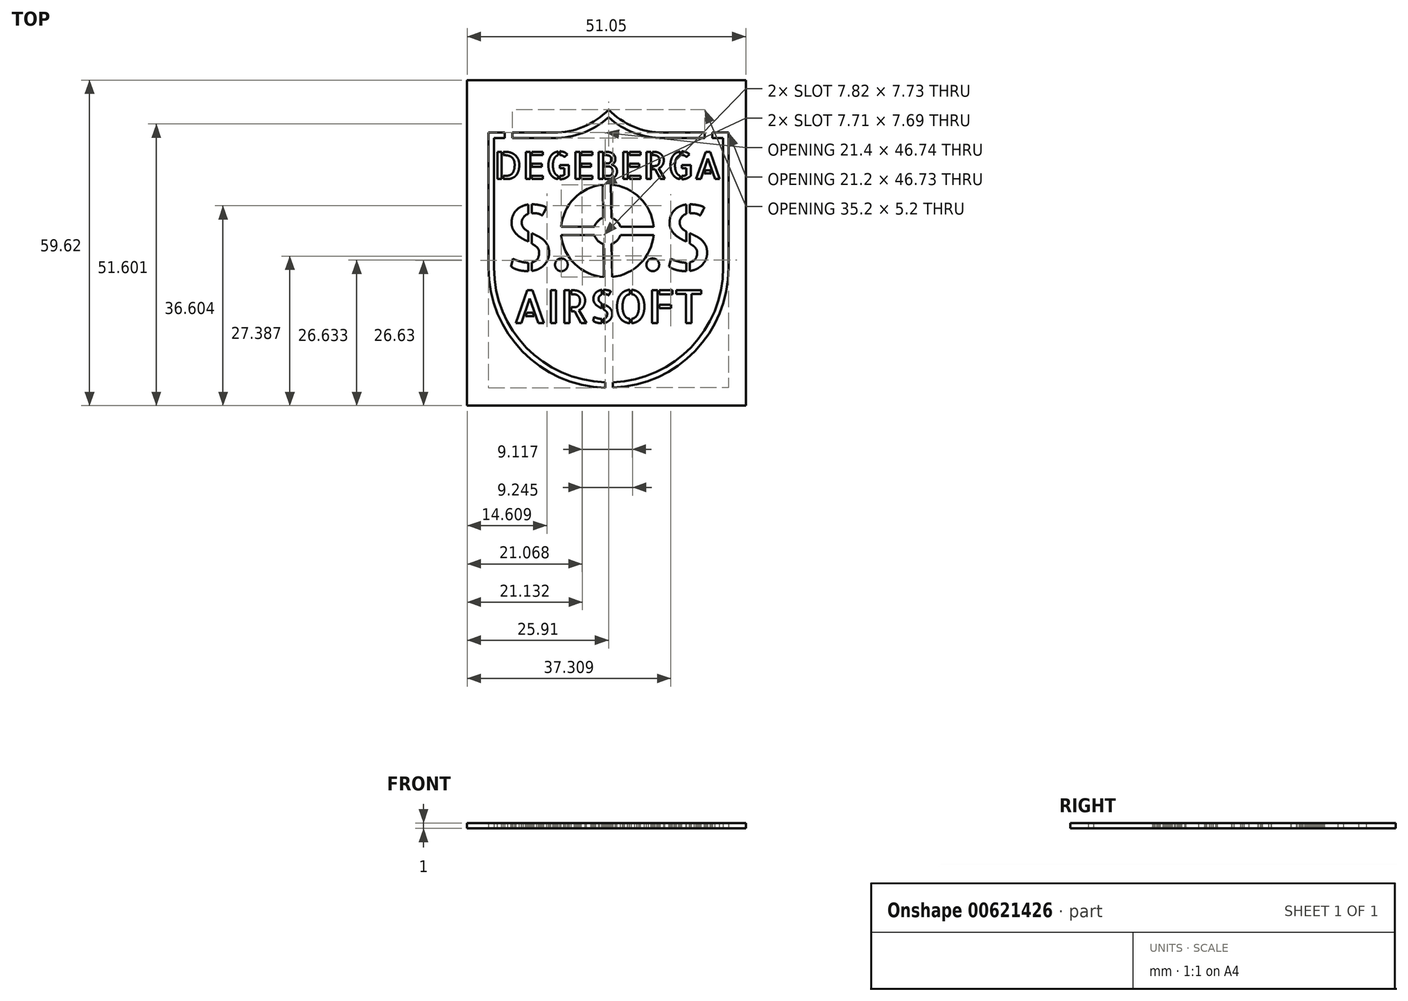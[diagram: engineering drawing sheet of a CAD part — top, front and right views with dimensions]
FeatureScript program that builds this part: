
annotation { "Feature Type Name" : "Feature", "Feature Type Description" : "" }
export const myFeature = defineFeature(function(context is Context, id is Id, definition is map)
    precondition{}
    {
        {
            var Q0;
            Q0=qCreatedBy(makeId("Top.planeOp"),FACE);
            var sketch = newSketch(context, id + "F0", { "sketchPlane" : qUnion([Q0])});
            skLineSegment(sketch, "E0.bottom", {"start": v(-46.46, 42.23) * mm, "end": v(53.54, 42.23) * mm});
            skLineSegment(sketch, "E0.top", {"start": v(-46.46, -77.77) * mm, "end": v(53.54, -77.77) * mm});
            skLineSegment(sketch, "E0.left", {"start": v(-46.46, 42.23) * mm, "end": v(-46.46, -77.77) * mm});
            skLineSegment(sketch, "E0.right", {"start": v(53.54, 42.23) * mm, "end": v(53.54, -77.77) * mm});
            skArc(sketch, "E1", {"start": v(-22, -24.75) * mm, "mid": v(-15.77, -40.09) * mm, "end": v(-0.6, -46.74) * mm});
            skLineSegment(sketch, "E2", {"start": v(-22, -24.75) * mm, "end": v(-22, 0) * mm});
            skLineSegment(sketch, "E3", {"start": v(22, -24.75) * mm, "end": v(22, 0) * mm});
            skLineSegment(sketch, "E4", {"start": v(-22, 0) * mm, "end": v(-19, 0) * mm});
            skLineSegment(sketch, "E5", {"start": v(22, 0) * mm, "end": v(19, 0) * mm});
            skArc(sketch, "E6", {"start": v(-10, 0) * mm, "mid": v(-4.58, 1.1) * mm, "end": v(0, 4.2) * mm});
            skArc(sketch, "E7", {"start": v(0, 4.2) * mm, "mid": v(4.58, 1.1) * mm, "end": v(10, 0) * mm});
            skArc(sketch, "E8", {"start": v(-21, -24.75) * mm, "mid": v(-15.06, -39.38) * mm, "end": v(-0.6, -45.74) * mm});
            skLineSegment(sketch, "E9", {"start": v(-21, -24.75) * mm, "end": v(-21, -1) * mm});
            skLineSegment(sketch, "E10", {"start": v(-21, -1) * mm, "end": v(-19, -1) * mm});
            skLineSegment(sketch, "E11", {"start": v(21, -24.75) * mm, "end": v(21, -1) * mm});
            skLineSegment(sketch, "E12", {"start": v(21, -1) * mm, "end": v(19, -1) * mm});
            skArc(sketch, "E13", {"start": v(-10, -1) * mm, "mid": v(-4.65, -0.01) * mm, "end": v(0, 2.82) * mm});
            skArc(sketch, "E14", {"start": v(0, 2.82) * mm, "mid": v(4.65, -0.01) * mm, "end": v(10, -1) * mm});
            skLineSegment(sketch, "E15.left", {"start": v(-19, 0) * mm, "end": v(-19, -1) * mm});
            skLineSegment(sketch, "E15.right", {"start": v(-17.6, 0) * mm, "end": v(-17.6, -1) * mm});
            skLineSegment(sketch, "E16.left", {"start": v(17.6, 0) * mm, "end": v(17.6, -1) * mm});
            skLineSegment(sketch, "E16.right", {"start": v(19, 0) * mm, "end": v(19, -1) * mm});
            skLineSegment(sketch, "E17", {"start": v(-0.6, -45.74) * mm, "end": v(-0.6, -46.74) * mm});
            skLineSegment(sketch, "E18", {"start": v(0.8, -45.73) * mm, "end": v(0.8, -46.73) * mm});
            skArc(sketch, "E19.trimOffspring", {"start": v(0.8, -45.73) * mm, "mid": v(15.13, -39.31) * mm, "end": v(21, -24.75) * mm});
            skArc(sketch, "E20.trimOffspring", {"start": v(0.8, -46.73) * mm, "mid": v(15.84, -40.02) * mm, "end": v(22, -24.75) * mm});
            skLineSegment(sketch, "E21.trimOffspring", {"start": v(17.6, -1) * mm, "end": v(10, -1) * mm});
            skLineSegment(sketch, "E22.trimOffspring", {"start": v(17.6, 0) * mm, "end": v(10, 0) * mm});
            skLineSegment(sketch, "E23.trimOffspring", {"start": v(-17.6, 0) * mm, "end": v(-10, 0) * mm});
            skLineSegment(sketch, "E24.trimOffspring", {"start": v(-17.6, -1) * mm, "end": v(-10, -1) * mm});
            skSolve(sketch);
        }
        {
            var Q0;
            Q0 = qSketchRegion(id + "F0", true);
            var Q1;
            Q1=makeQuery(id+"F0.imprint","IMPRINT",FACE,{"disambiguationData":[TD([[makeQuery(id+"F0.imprint","IMPRINT",EDGE,{"derivedFrom":sQuery(id+"F0.wireOp",EDGE,"E8")}),1.0]])]});
            extrude(context, id + "F1", {"entities" : qUnion([Q0, Q1]), "depth" : 1 * mm, "offsetDistance" : 25 * mm});
        }
        {
            var Q0;
            Q0=makeQuery(id+"F1.opExtrude","CAP_FACE",FACE,{"disambiguationData":[OSD([sQuery(id+"F0.wireOp",EDGE,"E0.bottom"),sQuery(id+"F0.wireOp",EDGE,"E0.top"),sQuery(id+"F0.wireOp",EDGE,"E0.left"),sQuery(id+"F0.wireOp",EDGE,"E0.right"),sQuery(id+"F0.wireOp",EDGE,"E1"),sQuery(id+"F0.wireOp",EDGE,"E2"),sQuery(id+"F0.wireOp",EDGE,"E3"),sQuery(id+"F0.wireOp",EDGE,"E4"),sQuery(id+"F0.wireOp",EDGE,"E5"),sQuery(id+"F0.wireOp",EDGE,"E6"),sQuery(id+"F0.wireOp",EDGE,"E7"),sQuery(id+"F0.wireOp",EDGE,"E8"),sQuery(id+"F0.wireOp",EDGE,"E9"),sQuery(id+"F0.wireOp",EDGE,"E10"),sQuery(id+"F0.wireOp",EDGE,"E11"),sQuery(id+"F0.wireOp",EDGE,"E12"),sQuery(id+"F0.wireOp",EDGE,"E13"),sQuery(id+"F0.wireOp",EDGE,"E14"),sQuery(id+"F0.wireOp",EDGE,"E15.left"),sQuery(id+"F0.wireOp",EDGE,"E15.right"),sQuery(id+"F0.wireOp",EDGE,"E16.left"),sQuery(id+"F0.wireOp",EDGE,"E16.right"),sQuery(id+"F0.wireOp",EDGE,"E17"),sQuery(id+"F0.wireOp",EDGE,"E18"),sQuery(id+"F0.wireOp",EDGE,"E19.trimOffspring"),sQuery(id+"F0.wireOp",EDGE,"E20.trimOffspring"),sQuery(id+"F0.wireOp",EDGE,"E21.trimOffspring"),sQuery(id+"F0.wireOp",EDGE,"E22.trimOffspring"),sQuery(id+"F0.wireOp",EDGE,"E23.trimOffspring"),sQuery(id+"F0.wireOp",EDGE,"E24.trimOffspring")])],"isStart":false});
            var sketch = newSketch(context, id + "F2", { "sketchPlane" : qUnion([Q0])});
            skText(sketch, "E25", { "text": "S.   .S", "fontName": "AllertaStencil-Regular.ttf"});
            const initialGuessF2  = {"E25": [-0.01917, -0.02531, 1, 0, 0.012]};
            skSetInitialGuess(sketch, initialGuessF2);
            skSolve(sketch);
        }
        {
            var Q0;
            Q0 = qSketchRegion(id + "F2", true);
            extrude(context, id + "F3", {"entities" : qUnion([Q0]), "operationType" : NewBodyOperationType.REMOVE, "oppositeDirection" : true, "depth" : 25 * mm, "offsetDistance" : 25 * mm});
        }
        {
            var Q0;
            Q0=makeQuery(id+"F1.opExtrude","CAP_FACE",FACE,{"disambiguationData":[OSD([sQuery(id+"F0.wireOp",EDGE,"E0.bottom"),sQuery(id+"F0.wireOp",EDGE,"E0.top"),sQuery(id+"F0.wireOp",EDGE,"E0.left"),sQuery(id+"F0.wireOp",EDGE,"E0.right"),sQuery(id+"F0.wireOp",EDGE,"E1"),sQuery(id+"F0.wireOp",EDGE,"E2"),sQuery(id+"F0.wireOp",EDGE,"E3"),sQuery(id+"F0.wireOp",EDGE,"E4"),sQuery(id+"F0.wireOp",EDGE,"E5"),sQuery(id+"F0.wireOp",EDGE,"E6"),sQuery(id+"F0.wireOp",EDGE,"E7"),sQuery(id+"F0.wireOp",EDGE,"E8"),sQuery(id+"F0.wireOp",EDGE,"E9"),sQuery(id+"F0.wireOp",EDGE,"E10"),sQuery(id+"F0.wireOp",EDGE,"E11"),sQuery(id+"F0.wireOp",EDGE,"E12"),sQuery(id+"F0.wireOp",EDGE,"E13"),sQuery(id+"F0.wireOp",EDGE,"E14"),sQuery(id+"F0.wireOp",EDGE,"E15.left"),sQuery(id+"F0.wireOp",EDGE,"E15.right"),sQuery(id+"F0.wireOp",EDGE,"E16.left"),sQuery(id+"F0.wireOp",EDGE,"E16.right"),sQuery(id+"F0.wireOp",EDGE,"E17"),sQuery(id+"F0.wireOp",EDGE,"E18"),sQuery(id+"F0.wireOp",EDGE,"E19.trimOffspring"),sQuery(id+"F0.wireOp",EDGE,"E20.trimOffspring"),sQuery(id+"F0.wireOp",EDGE,"E21.trimOffspring"),sQuery(id+"F0.wireOp",EDGE,"E22.trimOffspring"),sQuery(id+"F0.wireOp",EDGE,"E23.trimOffspring"),sQuery(id+"F0.wireOp",EDGE,"E24.trimOffspring")])],"isStart":false});
            var sketch = newSketch(context, id + "F4", { "sketchPlane" : qUnion([Q0])});
            skCircle(sketch, "E26", {"center": v(-0.22, -18) * mm, "radius": 8.5 * mm});
            skCircle(sketch, "E27", {"center": v(-0.22, -18) * mm, "radius": 2.5 * mm});
            skLineSegment(sketch, "E28.left", {"start": v(-1.07, -9.54) * mm, "end": v(-0.87, -26.48) * mm});
            skLineSegment(sketch, "E28.right", {"start": v(0.43, -9.52) * mm, "end": v(0.63, -26.46) * mm});
            skLineSegment(sketch, "E29.bottom", {"start": v(-8.69, -17.25) * mm, "end": v(8.25, -17.25) * mm});
            skLineSegment(sketch, "E29.top", {"start": v(-8.69, -18.75) * mm, "end": v(8.25, -18.75) * mm});
            skSolve(sketch);
        }
        {
            var Q0;
            {var subQ0=sQuery(id+"F4.wireOp",EDGE,"E28.right");var subQ1=sQuery(id+"F4.wireOp",EDGE,"E26");var subQ2=makeQuery(id+"F4.imprint","INTERSECT",VERTEX,{"disambiguationData":[OD(0.0)],"derivedFrom":[subQ1,subQ0]});Q0=makeQuery(id+"F4.imprint","IMPRINT",FACE,{"disambiguationData":[TD([[makeQuery(id+"F4.imprint","IMPRINT",EDGE,{"disambiguationData":[TD([[subQ2,1.0]])],"derivedFrom":subQ1}),1.0]])]});}
            var Q1;
            {var subQ0=sQuery(id+"F4.wireOp",EDGE,"E28.left");var subQ1=sQuery(id+"F4.wireOp",EDGE,"E26");var subQ2=makeQuery(id+"F4.imprint","INTERSECT",VERTEX,{"disambiguationData":[OD(0.0)],"derivedFrom":[subQ1,subQ0]});Q1=makeQuery(id+"F4.imprint","IMPRINT",FACE,{"disambiguationData":[TD([[makeQuery(id+"F4.imprint","IMPRINT",EDGE,{"disambiguationData":[TD([[subQ2,-1.0]])],"derivedFrom":subQ1}),1.0]])]});}
            var Q2;
            {var subQ0=sQuery(id+"F4.wireOp",EDGE,"E28.left");var subQ1=sQuery(id+"F4.wireOp",EDGE,"E26");var subQ2=makeQuery(id+"F4.imprint","INTERSECT",VERTEX,{"disambiguationData":[OD(1.0)],"derivedFrom":[subQ1,subQ0]});Q2=makeQuery(id+"F4.imprint","IMPRINT",FACE,{"disambiguationData":[TD([[makeQuery(id+"F4.imprint","IMPRINT",EDGE,{"disambiguationData":[TD([[subQ2,1.0]])],"derivedFrom":subQ1}),1.0]])]});}
            var Q3;
            {var subQ0=sQuery(id+"F4.wireOp",EDGE,"E28.right");var subQ1=sQuery(id+"F4.wireOp",EDGE,"E26");var subQ2=makeQuery(id+"F4.imprint","INTERSECT",VERTEX,{"disambiguationData":[OD(1.0)],"derivedFrom":[subQ1,subQ0]});Q3=makeQuery(id+"F4.imprint","IMPRINT",FACE,{"disambiguationData":[TD([[makeQuery(id+"F4.imprint","IMPRINT",EDGE,{"disambiguationData":[TD([[subQ2,-1.0]])],"derivedFrom":subQ1}),1.0]])]});}
            extrude(context, id + "F5", {"entities" : qUnion([Q0, Q1, Q2, Q3]), "operationType" : NewBodyOperationType.REMOVE, "oppositeDirection" : true, "depth" : 25 * mm, "offsetDistance" : 25 * mm});
        }
        {
            var Q0;
            Q0=makeQuery(id+"F1.opExtrude","CAP_FACE",FACE,{"disambiguationData":[OSD([sQuery(id+"F0.wireOp",EDGE,"E0.bottom"),sQuery(id+"F0.wireOp",EDGE,"E0.top"),sQuery(id+"F0.wireOp",EDGE,"E0.left"),sQuery(id+"F0.wireOp",EDGE,"E0.right"),sQuery(id+"F0.wireOp",EDGE,"E1"),sQuery(id+"F0.wireOp",EDGE,"E2"),sQuery(id+"F0.wireOp",EDGE,"E3"),sQuery(id+"F0.wireOp",EDGE,"E4"),sQuery(id+"F0.wireOp",EDGE,"E5"),sQuery(id+"F0.wireOp",EDGE,"E6"),sQuery(id+"F0.wireOp",EDGE,"E7"),sQuery(id+"F0.wireOp",EDGE,"E8"),sQuery(id+"F0.wireOp",EDGE,"E9"),sQuery(id+"F0.wireOp",EDGE,"E10"),sQuery(id+"F0.wireOp",EDGE,"E11"),sQuery(id+"F0.wireOp",EDGE,"E12"),sQuery(id+"F0.wireOp",EDGE,"E13"),sQuery(id+"F0.wireOp",EDGE,"E14"),sQuery(id+"F0.wireOp",EDGE,"E15.left"),sQuery(id+"F0.wireOp",EDGE,"E15.right"),sQuery(id+"F0.wireOp",EDGE,"E16.left"),sQuery(id+"F0.wireOp",EDGE,"E16.right"),sQuery(id+"F0.wireOp",EDGE,"E17"),sQuery(id+"F0.wireOp",EDGE,"E18"),sQuery(id+"F0.wireOp",EDGE,"E19.trimOffspring"),sQuery(id+"F0.wireOp",EDGE,"E20.trimOffspring"),sQuery(id+"F0.wireOp",EDGE,"E21.trimOffspring"),sQuery(id+"F0.wireOp",EDGE,"E22.trimOffspring"),sQuery(id+"F0.wireOp",EDGE,"E23.trimOffspring"),sQuery(id+"F0.wireOp",EDGE,"E24.trimOffspring")])],"isStart":false});
            var sketch = newSketch(context, id + "F6", { "sketchPlane" : qUnion([Q0])});
            skText(sketch, "E30", { "text": "DEGEBERGA", "fontName": "AllertaStencil-Regular.ttf"});
            const initialGuessF6  = {"E30": [-0.02104, -0.0085, 1, 0, 0.005]};
            skSetInitialGuess(sketch, initialGuessF6);
            skSolve(sketch);
        }
        {
            var Q0;
            Q0 = qSketchRegion(id + "F6", true);
            extrude(context, id + "F7", {"entities" : qUnion([Q0]), "operationType" : NewBodyOperationType.REMOVE, "oppositeDirection" : true, "depth" : 25 * mm, "offsetDistance" : 25 * mm});
        }
        {
            var Q0;
            Q0=makeQuery(id+"F1.opExtrude","CAP_FACE",FACE,{"disambiguationData":[OSD([sQuery(id+"F0.wireOp",EDGE,"E0.bottom"),sQuery(id+"F0.wireOp",EDGE,"E0.top"),sQuery(id+"F0.wireOp",EDGE,"E0.left"),sQuery(id+"F0.wireOp",EDGE,"E0.right"),sQuery(id+"F0.wireOp",EDGE,"E1"),sQuery(id+"F0.wireOp",EDGE,"E2"),sQuery(id+"F0.wireOp",EDGE,"E3"),sQuery(id+"F0.wireOp",EDGE,"E4"),sQuery(id+"F0.wireOp",EDGE,"E5"),sQuery(id+"F0.wireOp",EDGE,"E6"),sQuery(id+"F0.wireOp",EDGE,"E7"),sQuery(id+"F0.wireOp",EDGE,"E8"),sQuery(id+"F0.wireOp",EDGE,"E9"),sQuery(id+"F0.wireOp",EDGE,"E10"),sQuery(id+"F0.wireOp",EDGE,"E11"),sQuery(id+"F0.wireOp",EDGE,"E12"),sQuery(id+"F0.wireOp",EDGE,"E13"),sQuery(id+"F0.wireOp",EDGE,"E14"),sQuery(id+"F0.wireOp",EDGE,"E15.left"),sQuery(id+"F0.wireOp",EDGE,"E15.right"),sQuery(id+"F0.wireOp",EDGE,"E16.left"),sQuery(id+"F0.wireOp",EDGE,"E16.right"),sQuery(id+"F0.wireOp",EDGE,"E17"),sQuery(id+"F0.wireOp",EDGE,"E18"),sQuery(id+"F0.wireOp",EDGE,"E19.trimOffspring"),sQuery(id+"F0.wireOp",EDGE,"E20.trimOffspring"),sQuery(id+"F0.wireOp",EDGE,"E21.trimOffspring"),sQuery(id+"F0.wireOp",EDGE,"E22.trimOffspring"),sQuery(id+"F0.wireOp",EDGE,"E23.trimOffspring"),sQuery(id+"F0.wireOp",EDGE,"E24.trimOffspring")])],"isStart":false});
            var sketch = newSketch(context, id + "F8", { "sketchPlane" : qUnion([Q0])});
            skText(sketch, "E31", { "text": "AIRSOFT", "fontName": "AllertaStencil-Regular.ttf"});
            const initialGuessF8  = {"E31": [-0.01753, -0.03488, 1, 0, 0.006]};
            skSetInitialGuess(sketch, initialGuessF8);
            skSolve(sketch);
        }
        {
            var Q0;
            Q0 = qSketchRegion(id + "F8", true);
            extrude(context, id + "F9", {"entities" : qUnion([Q0]), "operationType" : NewBodyOperationType.REMOVE, "oppositeDirection" : true, "depth" : 25 * mm, "offsetDistance" : 25 * mm});
        }
        {
            var Q0;
            Q0=makeQuery(id+"F1.opExtrude","CAP_FACE",FACE,{"disambiguationData":[OSD([sQuery(id+"F0.wireOp",EDGE,"E0.bottom"),sQuery(id+"F0.wireOp",EDGE,"E0.top"),sQuery(id+"F0.wireOp",EDGE,"E0.left"),sQuery(id+"F0.wireOp",EDGE,"E0.right"),sQuery(id+"F0.wireOp",EDGE,"E1"),sQuery(id+"F0.wireOp",EDGE,"E2"),sQuery(id+"F0.wireOp",EDGE,"E3"),sQuery(id+"F0.wireOp",EDGE,"E4"),sQuery(id+"F0.wireOp",EDGE,"E5"),sQuery(id+"F0.wireOp",EDGE,"E6"),sQuery(id+"F0.wireOp",EDGE,"E7"),sQuery(id+"F0.wireOp",EDGE,"E8"),sQuery(id+"F0.wireOp",EDGE,"E9"),sQuery(id+"F0.wireOp",EDGE,"E10"),sQuery(id+"F0.wireOp",EDGE,"E11"),sQuery(id+"F0.wireOp",EDGE,"E12"),sQuery(id+"F0.wireOp",EDGE,"E13"),sQuery(id+"F0.wireOp",EDGE,"E14"),sQuery(id+"F0.wireOp",EDGE,"E15.left"),sQuery(id+"F0.wireOp",EDGE,"E15.right"),sQuery(id+"F0.wireOp",EDGE,"E16.left"),sQuery(id+"F0.wireOp",EDGE,"E16.right"),sQuery(id+"F0.wireOp",EDGE,"E17"),sQuery(id+"F0.wireOp",EDGE,"E18"),sQuery(id+"F0.wireOp",EDGE,"E19.trimOffspring"),sQuery(id+"F0.wireOp",EDGE,"E20.trimOffspring"),sQuery(id+"F0.wireOp",EDGE,"E21.trimOffspring"),sQuery(id+"F0.wireOp",EDGE,"E22.trimOffspring"),sQuery(id+"F0.wireOp",EDGE,"E23.trimOffspring"),sQuery(id+"F0.wireOp",EDGE,"E24.trimOffspring")])],"isStart":false});
            var sketch = newSketch(context, id + "F10", { "sketchPlane" : qUnion([Q0])});
            skLineSegment(sketch, "E32.bottom", {"start": v(-49.63, 43.22) * mm, "end": v(55.12, 43.22) * mm});
            skLineSegment(sketch, "E32.top", {"start": v(-49.63, 9.62) * mm, "end": v(55.12, 9.62) * mm});
            skLineSegment(sketch, "E32.left", {"start": v(-49.63, 43.22) * mm, "end": v(-49.63, 9.62) * mm});
            skLineSegment(sketch, "E32.right", {"start": v(55.12, 43.22) * mm, "end": v(55.12, 9.62) * mm});
            skLineSegment(sketch, "E33.bottom", {"start": v(-50.62, -80.14) * mm, "end": v(56.44, -80.14) * mm});
            skLineSegment(sketch, "E33.top", {"start": v(-50.62, -50) * mm, "end": v(56.44, -50) * mm});
            skLineSegment(sketch, "E33.left", {"start": v(-50.62, -80.14) * mm, "end": v(-50.62, -50) * mm});
            skLineSegment(sketch, "E33.right", {"start": v(56.44, -80.14) * mm, "end": v(56.44, -50) * mm});
            skLineSegment(sketch, "E34.bottom", {"start": v(58.58, -87.39) * mm, "end": v(25.14, -87.39) * mm});
            skLineSegment(sketch, "E34.top", {"start": v(58.58, 19.17) * mm, "end": v(25.14, 19.17) * mm});
            skLineSegment(sketch, "E34.left", {"start": v(58.58, -87.39) * mm, "end": v(58.58, 19.17) * mm});
            skLineSegment(sketch, "E34.right", {"start": v(25.14, -87.39) * mm, "end": v(25.14, 19.17) * mm});
            skLineSegment(sketch, "E35.bottom", {"start": v(-50.29, -86.24) * mm, "end": v(-25.91, -86.24) * mm});
            skLineSegment(sketch, "E35.top", {"start": v(-50.29, 18.51) * mm, "end": v(-25.91, 18.51) * mm});
            skLineSegment(sketch, "E35.left", {"start": v(-50.29, -86.24) * mm, "end": v(-50.29, 18.51) * mm});
            skLineSegment(sketch, "E35.right", {"start": v(-25.91, -86.24) * mm, "end": v(-25.91, 18.51) * mm});
            skSolve(sketch);
        }
        {
            var Q0;
            Q0 = qSketchRegion(id + "F10", true);
            extrude(context, id + "F11", {"entities" : qUnion([Q0]), "operationType" : NewBodyOperationType.REMOVE, "oppositeDirection" : true, "depth" : 25 * mm, "offsetDistance" : 25 * mm});
        }
    });
